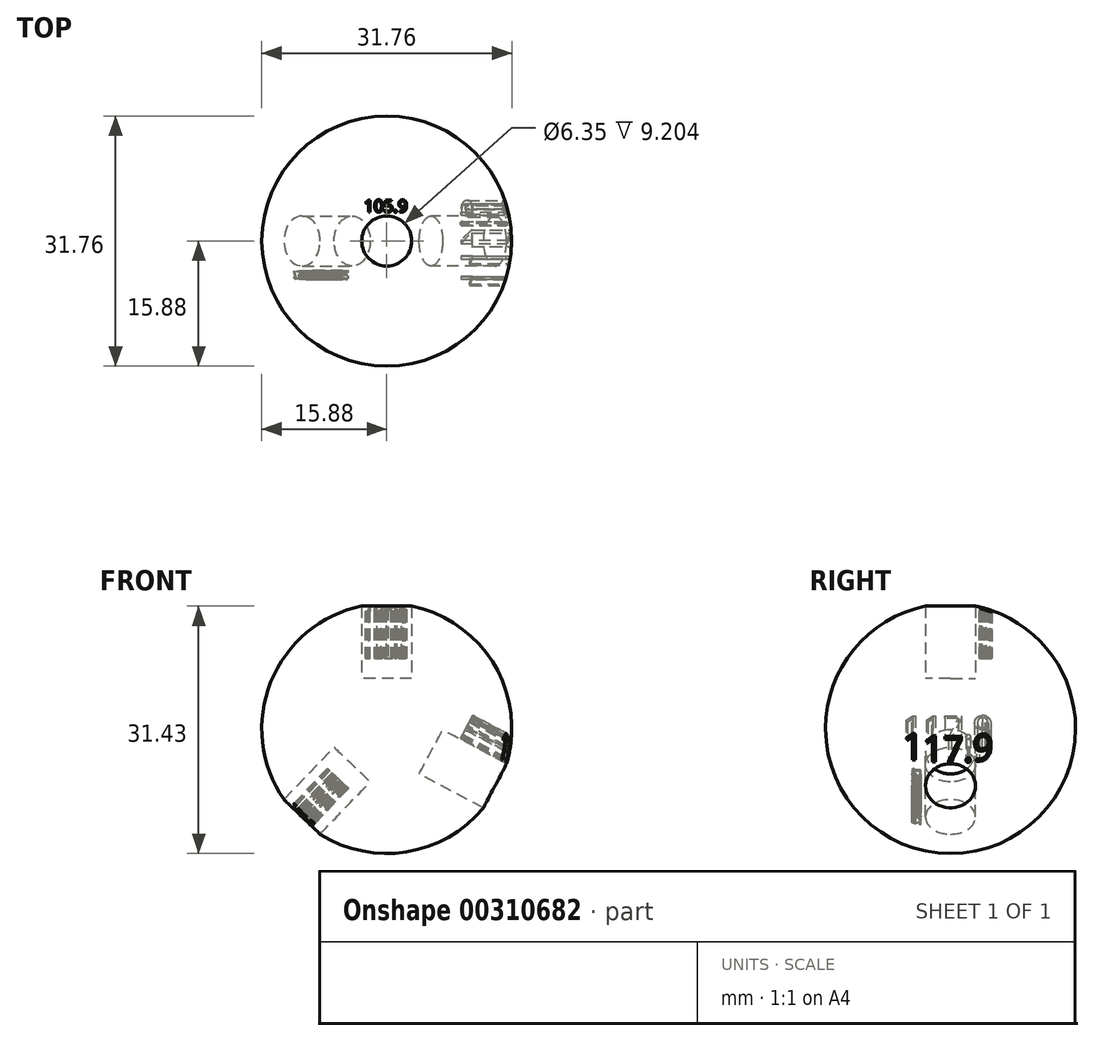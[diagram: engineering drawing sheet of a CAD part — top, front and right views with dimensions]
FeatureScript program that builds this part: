
annotation { "Feature Type Name" : "Feature", "Feature Type Description" : "" }
export const myFeature = defineFeature(function(context is Context, id is Id, definition is map)
    precondition{}
    {
        {
            var Q0;
            Q0=qCreatedBy(makeId("Right.planeOp"),FACE);
            var sketch = newSketch(context, id + "F0", { "sketchPlane" : qUnion([Q0])});
            skArc(sketch, "E0", {"start": v(-15.88, 0) * mm, "mid": v(0, -15.88) * mm, "end": v(15.88, 0) * mm});
            skLineSegment(sketch, "E1", {"start": v(15.88, 0) * mm, "end": v(-15.88, 0) * mm});
            skSolve(sketch);
        }
        {
            var Q0;
            Q0=qCreatedBy(makeId("Front.planeOp"),FACE);
            var sketch = newSketch(context, id + "F1", { "sketchPlane" : qUnion([Q0])});
            skCircle(sketch, "E2", {"center": v(0, 0) * mm, "radius": 15.88 * mm});
            skSolve(sketch);
        }
        {
            var Q0;
            Q0 = qSketchRegion(id + "F0", true);
            var Q1;
            Q1=sQuery(id+"F1.wireOp",EDGE,"E2");
            revolve(context, id + "F2", {"entities" : qUnion([Q0]), "axis" : qUnion([Q1]), "revolveType" : RevolveType.FULL});
        }
        {
            var Q0;
            Q0=qCreatedBy(makeId("Top.planeOp"),FACE);
            cPlane(context, id + "F3", {"entities" : qUnion([Q0]), "cplaneType" : CPlaneType.OFFSET, "offset" : 6.35 * mm, "width" : 152.4 * mm, "height" : 152.4 * mm});
        }
        {
            var Q0;
            Q0=qCreatedBy(id+"F3.planeOp",FACE);
            var sketch = newSketch(context, id + "F4", { "sketchPlane" : qUnion([Q0])});
            skCircle(sketch, "E3", {"center": v(0, 0) * mm, "radius": 3.18 * mm});
            skSolve(sketch);
        }
        {
            var Q0;
            Q0 = qSketchRegion(id + "F4", true);
            extrude(context, id + "F5", {"entities" : qUnion([Q0]), "depth" : 25.4 * mm});
        }
        {
            var Q0;
            Q0=makeQuery(id+"F5.opExtrude","CAP_FACE",FACE,{"disambiguationData":[OSD([sQuery(id+"F4.wireOp",EDGE,"E3")])],"isStart":false});
            cPlane(context, id + "F6", {"entities" : qUnion([Q0]), "cplaneType" : CPlaneType.OFFSET, "offset" : 12.7 * mm, "oppositeDirection" : true, "width" : 152.4 * mm, "height" : 152.4 * mm});
        }
        {
            var Q0;
            Q0=qCreatedBy(id+"F6.planeOp",FACE);
            var sketch = newSketch(context, id + "F7", { "sketchPlane" : qUnion([Q0])});
            skText(sketch, "E4", { "text": "105.9\n", "fontName": "OpenSans-Regular.ttf"});
            const initialGuessF7  = {"E4": [-0.00288, 0.00367, 1, 0, 0.00156]};
            skSetInitialGuess(sketch, initialGuessF7);
            skSolve(sketch);
        }
        {
            var Q0;
            Q0 = qSketchRegion(id + "F7", true);
            extrude(context, id + "F8", {"entities" : qUnion([Q0]), "operationType" : NewBodyOperationType.REMOVE, "oppositeDirection" : true, "depth" : 10.16 * mm});
        }
        {
            var Q0;
            Q0=qCreatedBy(makeId("Right.planeOp"),FACE);
            var sketch = newSketch(context, id + "F9", { "sketchPlane" : qUnion([Q0])});
            skLineSegment(sketch, "E5", {"start": v(-63.23, 0) * mm, "end": v(60.65, 0) * mm, "construction": true});
            skSolve(sketch);
        }
        {
            var Q0;
            Q0=makeQuery(id+"F5.opExtrude","SWEPT_BODY",BODY,{"disambiguationData":[OSD([sQuery(id+"F4.wireOp",EDGE,"E3")])]});
            var Q1;
            Q1=sQuery(id+"F9.wireOp",EDGE,"E5");
            var Q2;
            Q2=sQuery(id+"F9.wireOp",EDGE,"E5");
            transform(context, id + "F10", {"entities" : qUnion([Q0]), "transformType" : TransformType.ROTATION, "transformAxis" : qUnion([Q2]), "angle" : 117.9 * degree, "makeCopy" : true});
        }
        {
            var Q0;
            Q0=makeQuery(id+"F10.opPattern","COPY",FACE,{"derivedFrom":makeQuery(id+"F5.opExtrude","CAP_FACE",FACE,{"disambiguationData":[OSD([sQuery(id+"F4.wireOp",EDGE,"E3")])],"isStart":false}),"instanceName":"1"});
            cPlane(context, id + "F11", {"entities" : qUnion([Q0]), "cplaneType" : CPlaneType.OFFSET, "offset" : 12.7 * mm, "oppositeDirection" : true, "width" : 152.4 * mm, "height" : 152.4 * mm});
        }
        {
            var Q0;
            Q0=qCreatedBy(id+"F11.planeOp",FACE);
            var sketch = newSketch(context, id + "F12", { "sketchPlane" : qUnion([Q0])});
            skText(sketch, "E6", { "text": "117.9\n", "fontName": "OpenSans-Regular.ttf"});
            const initialGuessF12  = {"E6": [-0.00606, 0.00332, 1, 0, 0.00323]};
            skSetInitialGuess(sketch, initialGuessF12);
            skSolve(sketch);
        }
        {
            var Q0;
            Q0 = qSketchRegion(id + "F12", true);
            extrude(context, id + "F13", {"entities" : qUnion([Q0]), "operationType" : NewBodyOperationType.REMOVE, "oppositeDirection" : true, "depth" : 10.16 * mm});
        }
        {
            var Q0;
            Q0=qCreatedBy(makeId("Right.planeOp"),FACE);
            var sketch = newSketch(context, id + "F14", { "sketchPlane" : qUnion([Q0])});
            skLineSegment(sketch, "E7", {"start": v(-62.86, 0) * mm, "end": v(59.18, 0) * mm, "construction": true});
            skSolve(sketch);
        }
        {
            var Q0;
            Q0=makeQuery(id+"F5.opExtrude","SWEPT_BODY",BODY,{"disambiguationData":[OSD([sQuery(id+"F4.wireOp",EDGE,"E3")])]});
            var Q1;
            Q1=sQuery(id+"F14.wireOp",EDGE,"E7");
            transform(context, id + "F15", {"entities" : qUnion([Q0]), "transformType" : TransformType.ROTATION, "transformAxis" : qUnion([Q1]), "angle" : 136.2 * degree, "oppositeDirection" : true, "makeCopy" : true});
        }
        {
            var Q0;
            Q0=makeQuery(id+"F15.opPattern","COPY",FACE,{"derivedFrom":makeQuery(id+"F5.opExtrude","CAP_FACE",FACE,{"disambiguationData":[OSD([sQuery(id+"F4.wireOp",EDGE,"E3")])],"isStart":false}),"instanceName":"1"});
            cPlane(context, id + "F16", {"entities" : qUnion([Q0]), "cplaneType" : CPlaneType.OFFSET, "offset" : 12.7 * mm, "oppositeDirection" : true, "width" : 152.4 * mm, "height" : 152.4 * mm});
        }
        {
            var Q0;
            Q0=qCreatedBy(id+"F16.planeOp",FACE);
            var sketch = newSketch(context, id + "F17", { "sketchPlane" : qUnion([Q0])});
            skText(sketch, "E8", { "text": "136.2\n", "fontName": "OpenSans-Regular.ttf"});
            const initialGuessF17  = {"E8": [-0.00206, 0.0038, 1, 0, 0.0011]};
            skSetInitialGuess(sketch, initialGuessF17);
            skSolve(sketch);
        }
        {
            var Q0;
            Q0 = qSketchRegion(id + "F17", true);
            extrude(context, id + "F18", {"entities" : qUnion([Q0]), "operationType" : NewBodyOperationType.REMOVE, "oppositeDirection" : true, "depth" : 10.16 * mm});
        }
        {
            var Q0;
            Q0=makeQuery(id+"F5.opExtrude","SWEPT_BODY",BODY,{"disambiguationData":[OSD([sQuery(id+"F4.wireOp",EDGE,"E3")])]});
            var Q1;
            Q1=makeQuery(id+"F15.opPattern","COPY",BODY,{"derivedFrom":makeQuery(id+"F5.opExtrude","SWEPT_BODY",BODY,{"disambiguationData":[OSD([sQuery(id+"F4.wireOp",EDGE,"E3")])]}),"instanceName":"1"});
            var Q2;
            Q2=makeQuery(id+"F10.opPattern","COPY",BODY,{"derivedFrom":makeQuery(id+"F5.opExtrude","SWEPT_BODY",BODY,{"disambiguationData":[OSD([sQuery(id+"F4.wireOp",EDGE,"E3")])]}),"instanceName":"1"});
            var Q3;
            Q3=makeQuery(id+"F2.opRevolve","SWEPT_BODY",BODY,{"disambiguationData":[OSD([sQuery(id+"F0.wireOp",EDGE,"E0"),sQuery(id+"F0.wireOp",EDGE,"E1")])]});
            booleanBodies(context, id + "F19", {"operationType" : BooleanOperationType.SUBTRACTION, "tools" : qUnion([Q0, Q1, Q2]), "targets" : qUnion([Q3])});
        }
    });
